# Revit family: Shower-Valve_Trim-KOHLER-COMPONENTS-K-77980T
name_source: partatom
category: Specialty Equipment
revit_build: Autodesk Revit 2017 (Build: 20160225_1515(x64)
units: mm (PartAtom-declared; Revit-internal decimal feet)

## family parameters
Cut with Voids When Loaded = No
Host = Face
OmniClass Number = 23.31.25.00
OmniClass Title = Toilet and Bath Specialties
Part Type = Normal
Room Calculation Point = No
Round Connector Dimension = Use Diameter
Shared = No

## types (14) — shared parameters
ADA Compliant = No
Assembly Code = C1030200
Date Modified = 10/16/2020
Default Elevation = 42"
Height = 2 3/8"
Manufacturer = KOHLER Co.
Master Format 2014 = 10 28 00
Master Format 2014 Name = Toilet, Bath, and Laundry Accessories
Material = Premium Metal Construction
Product Documentation Link = https://files.kohler.com.cn
Product Name = COMPONENTS
Product Page URL = https://www.kohler.com.cn
URL = http://www.kohler.com.cn
WaterSense Certified = No
Width = 2 3/8"

## per-type parameters (varying)
| type | Description | Dist1 | Finish | Handle Clearance | Length | Lever Handle | Model | Pin Handle | Type |
| Lever Handle, CP-Polished Chrome | Single lever wall outlet basin faucet handle lever type | 11/16" | Kohler-Metal-CP-Polished_Chrome | 2 13/16" | 3 1/2" | Yes | K-77980T-4-CP | No | 1 |
| Lever Handle, AF-Flange Gold | Single lever wall outlet basin faucet handle lever type | 11/16" | Kohler-Metal-AF-Flange_Gold | 2 13/16" | 3 1/2" | Yes | K-77980T-4-AF | No | 2 |
| Lever Handle, BN-Roman Silver | Single lever wall outlet basin faucet handle lever type | 11/16" | Kohler-Metal-BN-Roman_Silver | 2 13/16" | 3 1/2" | Yes | K-77980T-4-BN | No | 3 |
| Lever Handle, RGD-Rose Gold | Single lever wall outlet basin faucet handle lever type | 11/16" | Kohler-Metal-RGD-Rose_Gold | 2 13/16" | 3 1/2" | Yes | K-77980T-4-RGD | No | 4 |
| Lever Handle, 2BL-Original Black | Single lever wall outlet basin faucet handle lever type | 11/16" | Kohler-Metal-2BL-Original_Black | 2 13/16" | 3 1/2" | Yes | K-77980T-4-2BL | No | 5 |
| Lever Handle, TT-Titanium Silver | Single lever wall outlet basin faucet handle lever type | 11/16" | Kohler-Metal-TT-Titanium_Silver | 2 13/16" | 3 1/2" | Yes | K-77980T-4-TT | No | 6 |
| Lever Handle, 2MB-Vibrant Brushed Moderne Brass | Single lever wall outlet basin faucet handle lever type | 11/16" | Kohler-Metal-2MB-Vibrant_Brushed_Moderne_Brass | 2 13/16" | 3 1/2" | Yes | K-77980T-4-2MB | No | 7 |
| Pin Handle, CP-Polished Chrome | Single handle wall outlet basin faucet handle thin rod type | 5/16" | Kohler-Metal-CP-Polished_Chrome | 3 9/16" | 3 1/8" | No | K-77980T-4A-CP | Yes | 8 |
| Pin Handle, AF-Flange Gold | Single handle wall outlet basin faucet handle thin rod type | 5/16" | Kohler-Metal-AF-Flange_Gold | 3 9/16" | 3 1/8" | No | K-77980T-4A-AF | Yes | 9 |
| Pin Handle, BN-Roman Silver | Single handle wall outlet basin faucet handle thin rod type | 5/16" | Kohler-Metal-BN-Roman_Silver | 3 9/16" | 3 1/8" | No | K-77980T-4A-BN | Yes | 10 |
| Pin Handle, RGD-Rose Gold | Single handle wall outlet basin faucet handle thin rod type | 5/16" | Kohler-Metal-RGD-Rose_Gold | 3 9/16" | 3 1/8" | No | K-77980T-4A-RGD | Yes | 11 |
| Pin Handle, 2BL-Original Black | Single handle wall outlet basin faucet handle thin rod type | 5/16" | Kohler-Metal-2BL-Original_Black | 3 9/16" | 3 1/8" | No | K-77980T-4A-2BL | Yes | 12 |
| Pin Handle, TT-Titanium Silver | Single handle wall outlet basin faucet handle thin rod type | 5/16" | Kohler-Metal-TT-Titanium_Silver | 3 9/16" | 3 1/8" | No | K-77980T-4A-TT | Yes | 13 |
| Pin Handle, 2MB-Vibrant Brushed Moderne Brass | Single handle wall outlet basin faucet handle thin rod type | 5/16" | Kohler-Metal-2MB-Vibrant_Brushed_Moderne_Brass | 3 9/16" | 3 1/8" | No | K-77980T-4A-2MB | Yes | 14 |

## geometry (parser evidence)
native form markers: Sweep x6
no freeform markers — native parametric forms only
